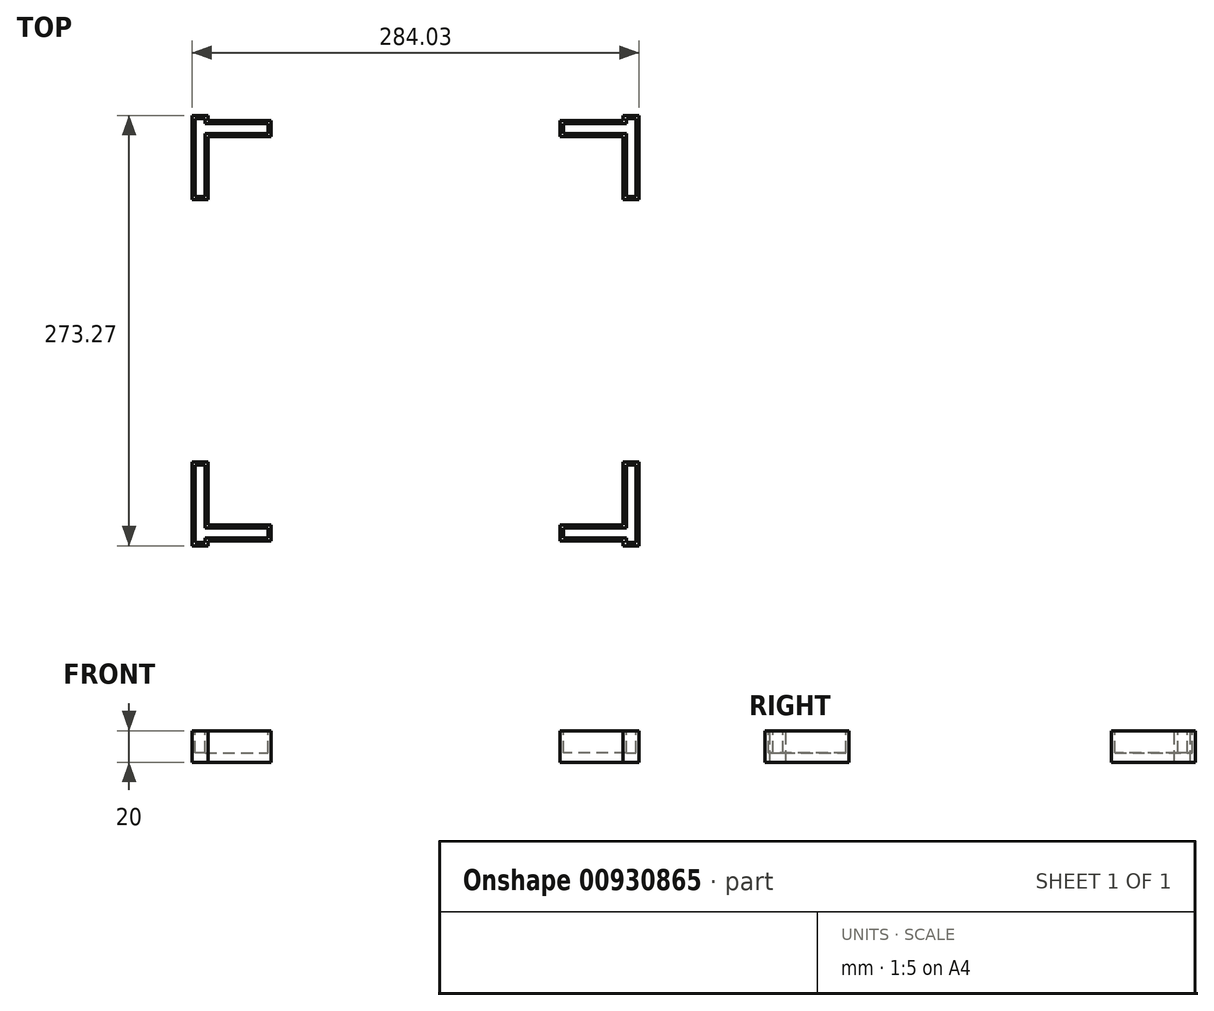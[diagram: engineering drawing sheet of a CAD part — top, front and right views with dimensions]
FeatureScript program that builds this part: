
annotation { "Feature Type Name" : "Feature", "Feature Type Description" : "" }
export const myFeature = defineFeature(function(context is Context, id is Id, definition is map)
    precondition{}
    {
        {
            var Q0;
            Q0=qCreatedBy(makeId("Top.planeOp"),FACE);
            var sketch = newSketch(context, id + "F0", { "sketchPlane" : qUnion([Q0])});
            skLineSegment(sketch, "E0", {"start": v(0, 49.3) * mm, "end": v(0, 0) * mm});
            skLineSegment(sketch, "E1", {"start": v(0, 0) * mm, "end": v(6.2, 0) * mm});
            skLineSegment(sketch, "E2", {"start": v(6.2, 0) * mm, "end": v(6.2, 3.1) * mm});
            skLineSegment(sketch, "E3", {"start": v(6.2, 3.1) * mm, "end": v(46.2, 3.1) * mm});
            skLineSegment(sketch, "E4", {"start": v(46.2, 3.1) * mm, "end": v(46.2, 9.3) * mm});
            skLineSegment(sketch, "E5", {"start": v(46.2, 9.3) * mm, "end": v(6.2, 9.3) * mm});
            skLineSegment(sketch, "E6", {"start": v(6.2, 9.3) * mm, "end": v(6.2, 49.3) * mm});
            skLineSegment(sketch, "E7", {"start": v(6.2, 49.3) * mm, "end": v(0, 49.3) * mm});
            skSolve(sketch);
        }
        {
            var Q0;
            Q0=qCreatedBy(makeId("Top.planeOp"),FACE);
            var sketch = newSketch(context, id + "F1", { "sketchPlane" : qUnion([Q0])});
            skLineSegment(sketch, "E8.bottom", {"start": v(48.2, -2) * mm, "end": v(-2, -2) * mm});
            skLineSegment(sketch, "E8.top", {"start": v(48.2, 51.3) * mm, "end": v(-2, 51.3) * mm});
            skLineSegment(sketch, "E8.left", {"start": v(48.2, -2) * mm, "end": v(48.2, 51.3) * mm});
            skLineSegment(sketch, "E8.right", {"start": v(-2, -2) * mm, "end": v(-2, 51.3) * mm});
            skPoint(sketch, "E8.middle", {"position": v(23.1, 24.65) * mm});
            skSolve(sketch);
        }
        {
            var Q0;
            Q0=makeQuery(id+"F1.imprint","IMPRINT",FACE,{"disambiguationData":[TD([[makeQuery(id+"F1.imprint","IMPRINT",EDGE,{"derivedFrom":sQuery(id+"F1.wireOp",EDGE,"E8.bottom")}),-1.0]])]});
            extrude(context, id + "F2", {"entities" : qUnion([Q0]), "oppositeDirection" : true, "depth" : 20 * mm, "offsetDistance" : 25 * mm});
        }
        {
            var Q0;
            Q0=makeQuery(id+"F0.imprint","IMPRINT",FACE,{"disambiguationData":[TD([[makeQuery(id+"F0.imprint","IMPRINT",EDGE,{"derivedFrom":sQuery(id+"F0.wireOp",EDGE,"E0")}),1.0]])]});
            extrude(context, id + "F3", {"entities" : qUnion([Q0]), "operationType" : NewBodyOperationType.REMOVE, "oppositeDirection" : true, "depth" : 14 * mm, "offsetDistance" : 25 * mm});
        }
        {
            var Q0;
            Q0=makeQuery(id+"F2.opExtrude","CAP_FACE",FACE,{"disambiguationData":[OSD([sQuery(id+"F1.wireOp",EDGE,"E8.bottom"),sQuery(id+"F1.wireOp",EDGE,"E8.top"),sQuery(id+"F1.wireOp",EDGE,"E8.left"),sQuery(id+"F1.wireOp",EDGE,"E8.right")])],"isStart":true});
            var sketch = newSketch(context, id + "F4", { "sketchPlane" : qUnion([Q0])});
            skLineSegment(sketch, "E9.bottom", {"start": v(48.2, 51.3) * mm, "end": v(8.2, 51.3) * mm});
            skLineSegment(sketch, "E9.top", {"start": v(48.2, 11.3) * mm, "end": v(8.2, 11.3) * mm});
            skLineSegment(sketch, "E9.left", {"start": v(48.2, 51.3) * mm, "end": v(48.2, 11.3) * mm});
            skLineSegment(sketch, "E9.right", {"start": v(8.2, 51.3) * mm, "end": v(8.2, 11.3) * mm});
            skLineSegment(sketch, "E10.bottom", {"start": v(48.2, -2) * mm, "end": v(8.2, -2) * mm});
            skLineSegment(sketch, "E10.top", {"start": v(48.2, 1.1) * mm, "end": v(8.2, 1.1) * mm});
            skLineSegment(sketch, "E10.left", {"start": v(48.2, -2) * mm, "end": v(48.2, 1.1) * mm});
            skLineSegment(sketch, "E10.right", {"start": v(8.2, -2) * mm, "end": v(8.2, 1.1) * mm});
            skSolve(sketch);
        }
        {
            var Q0;
            Q0 = qSketchRegion(id + "F4", true);
            extrude(context, id + "F5", {"entities" : qUnion([Q0]), "operationType" : NewBodyOperationType.REMOVE, "endBound" : BoundingType.THROUGH_ALL, "oppositeDirection" : true, "depth" : 25 * mm, "offsetDistance" : 25 * mm});
        }
        {
            var Q0;
            Q0=qCreatedBy(makeId("Top.planeOp"),FACE);
            var sketch = newSketch(context, id + "F6", { "sketchPlane" : qUnion([Q0])});
            skLineSegment(sketch, "E11", {"start": v(140.02, 212.34) * mm, "end": v(140.02, 56.93) * mm, "construction": true});
            skLineSegment(sketch, "E12", {"start": v(-12.99, 102.61) * mm, "end": v(325.61, 102.61) * mm, "construction": true});
            skSolve(sketch);
        }
        {
            var Q0;
            Q0=sQuery(id+"F6.wireOp",EDGE,"E11");
            cPlane(context, id + "F7", {"entities" : qUnion([Q0]), "cplaneType" : CPlaneType.MID_PLANE, "offset" : 25 * mm, "width" : 150 * mm, "height" : 150 * mm});
        }
        {
            var Q0;
            Q0=sQuery(id+"F6.wireOp",EDGE,"E11");
            cPlane(context, id + "F8", {"entities" : qUnion([Q0]), "cplaneType" : CPlaneType.LINE_ANGLE, "offset" : 25 * mm, "angle" : 90 * degree, "width" : 150 * mm, "height" : 150 * mm});
        }
        {
            var Q0;
            Q0=makeQuery(id+"F2.opExtrude","SWEPT_BODY",BODY,{"disambiguationData":[OSD([sQuery(id+"F1.wireOp",EDGE,"E8.bottom"),sQuery(id+"F1.wireOp",EDGE,"E8.top"),sQuery(id+"F1.wireOp",EDGE,"E8.left"),sQuery(id+"F1.wireOp",EDGE,"E8.right")])]});
            var Q1;
            Q1=qCreatedBy(id+"F8.planeOp",FACE);
            mirror(context, id + "F9", {"entities" : qUnion([Q0]), "mirrorPlane" : qUnion([Q1])});
        }
        {
            var Q0;
            Q0=makeQuery(id+"F2.opExtrude","SWEPT_BODY",BODY,{"disambiguationData":[OSD([sQuery(id+"F1.wireOp",EDGE,"E8.bottom"),sQuery(id+"F1.wireOp",EDGE,"E8.top"),sQuery(id+"F1.wireOp",EDGE,"E8.left"),sQuery(id+"F1.wireOp",EDGE,"E8.right")])]});
            var Q1;
            Q1=makeQuery(id+"F9.opPattern","COPY",BODY,{"derivedFrom":makeQuery(id+"F2.opExtrude","SWEPT_BODY",BODY,{"disambiguationData":[OSD([sQuery(id+"F1.wireOp",EDGE,"E8.bottom"),sQuery(id+"F1.wireOp",EDGE,"E8.top"),sQuery(id+"F1.wireOp",EDGE,"E8.left"),sQuery(id+"F1.wireOp",EDGE,"E8.right")])]}),"instanceName":"1"});
            var Q2;
            Q2=qCreatedBy(id+"F7.planeOp",FACE);
            mirror(context, id + "F10", {"entities" : qUnion([Q0, Q1]), "mirrorPlane" : qUnion([Q2])});
        }
    });
